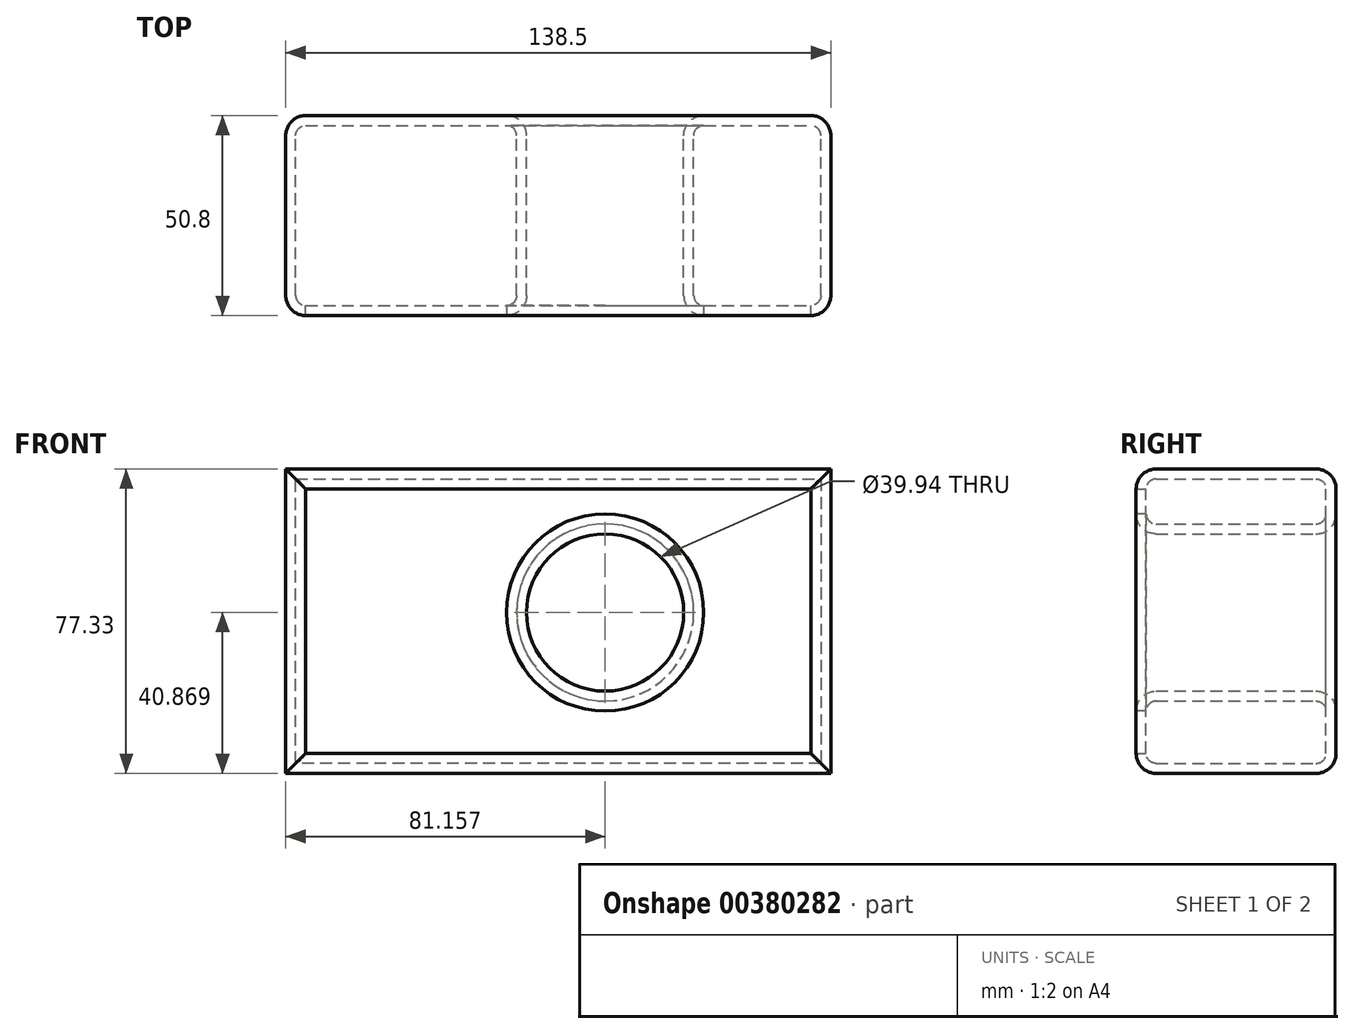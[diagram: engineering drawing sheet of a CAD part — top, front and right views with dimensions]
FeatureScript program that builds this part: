
annotation { "Feature Type Name" : "Feature", "Feature Type Description" : "" }
export const myFeature = defineFeature(function(context is Context, id is Id, definition is map)
    precondition{}
    {
        {
            var Q0;
            Q0=qCreatedBy(makeId("Front.planeOp"),FACE);
            var sketch = newSketch(context, id + "F0", { "sketchPlane" : qUnion([Q0])});
            skLineSegment(sketch, "E0", {"start": v(-71.86, -24.55) * mm, "end": v(-71.86, 52.78) * mm});
            skLineSegment(sketch, "E1", {"start": v(-71.86, 52.78) * mm, "end": v(66.64, 52.78) * mm});
            skLineSegment(sketch, "E2", {"start": v(66.64, 52.78) * mm, "end": v(66.64, -24.55) * mm});
            skLineSegment(sketch, "E3", {"start": v(66.64, -24.55) * mm, "end": v(-71.86, -24.55) * mm});
            skCircle(sketch, "E4", {"center": v(9.3, 16.32) * mm, "radius": 19.97 * mm});
            skSolve(sketch);
        }
        {
            var Q0;
            Q0=makeQuery(id+"F0.imprint","IMPRINT",FACE,{"disambiguationData":[TD([[makeQuery(id+"F0.imprint","IMPRINT",EDGE,{"derivedFrom":sQuery(id+"F0.wireOp",EDGE,"E0")}),-1.0]])]});
            extrude(context, id + "F1", {"entities" : qUnion([Q0]), "depth" : 50.8 * mm});
        }
        {
            var Q0;
            Q0=makeQuery(id+"F1.opExtrude","CAP_EDGE",EDGE,{"disambiguationData":[OSD([sQuery(id+"F0.wireOp",EDGE,"E2")])],"isStart":true});
            var Q1;
            Q1=makeQuery(id+"F1.opExtrude","CAP_EDGE",EDGE,{"disambiguationData":[OSD([sQuery(id+"F0.wireOp",EDGE,"E1")])],"isStart":true});
            var Q2;
            Q2=makeQuery(id+"F1.opExtrude","CAP_EDGE",EDGE,{"disambiguationData":[OSD([sQuery(id+"F0.wireOp",EDGE,"E0")])],"isStart":true});
            var Q3;
            Q3=makeQuery(id+"F1.opExtrude","CAP_EDGE",EDGE,{"disambiguationData":[OSD([sQuery(id+"F0.wireOp",EDGE,"E3")])],"isStart":true});
            var Q4;
            Q4=makeQuery(id+"F1.opExtrude","CAP_EDGE",EDGE,{"disambiguationData":[OSD([sQuery(id+"F0.wireOp",EDGE,"E4")])],"isStart":true});
            var Q5;
            Q5=makeQuery(id+"F1.opExtrude","CAP_EDGE",EDGE,{"disambiguationData":[OSD([sQuery(id+"F0.wireOp",EDGE,"E4")])],"isStart":false});
            fillet(context, id + "F2", {"entities" : qUnion([Q0, Q1, Q2, Q3, Q4, Q5]), "radius" : 5.08 * mm, "tangentPropagation" : true, "allowEdgeOverflow" : false});
        }
        {
            var Q0;
            Q0=makeQuery(id+"F1.opExtrude","CAP_EDGE",EDGE,{"disambiguationData":[OSD([sQuery(id+"F0.wireOp",EDGE,"E3")])],"isStart":false});
            var Q1;
            Q1=makeQuery(id+"F1.opExtrude","CAP_EDGE",EDGE,{"disambiguationData":[OSD([sQuery(id+"F0.wireOp",EDGE,"E0")])],"isStart":false});
            var Q2;
            Q2=makeQuery(id+"F1.opExtrude","CAP_EDGE",EDGE,{"disambiguationData":[OSD([sQuery(id+"F0.wireOp",EDGE,"E1")])],"isStart":false});
            var Q3;
            Q3=makeQuery(id+"F1.opExtrude","CAP_EDGE",EDGE,{"disambiguationData":[OSD([sQuery(id+"F0.wireOp",EDGE,"E2")])],"isStart":false});
            fillet(context, id + "F3", {"entities" : qUnion([Q0, Q1, Q2, Q3]), "radius" : 5.08 * mm, "tangentPropagation" : true, "allowEdgeOverflow" : false});
        }
        {
            var Q0;
            Q0=makeQuery(id+"F1.opExtrude","CAP_FACE",FACE,{"disambiguationData":[OSD([sQuery(id+"F0.wireOp",EDGE,"E0"),sQuery(id+"F0.wireOp",EDGE,"E1"),sQuery(id+"F0.wireOp",EDGE,"E2"),sQuery(id+"F0.wireOp",EDGE,"E3"),sQuery(id+"F0.wireOp",EDGE,"E4")])],"isStart":false});
            shell(context, id + "F4", {"entities" : qUnion([Q0]), "thickness" : 2.54 * mm});
        }
    });
